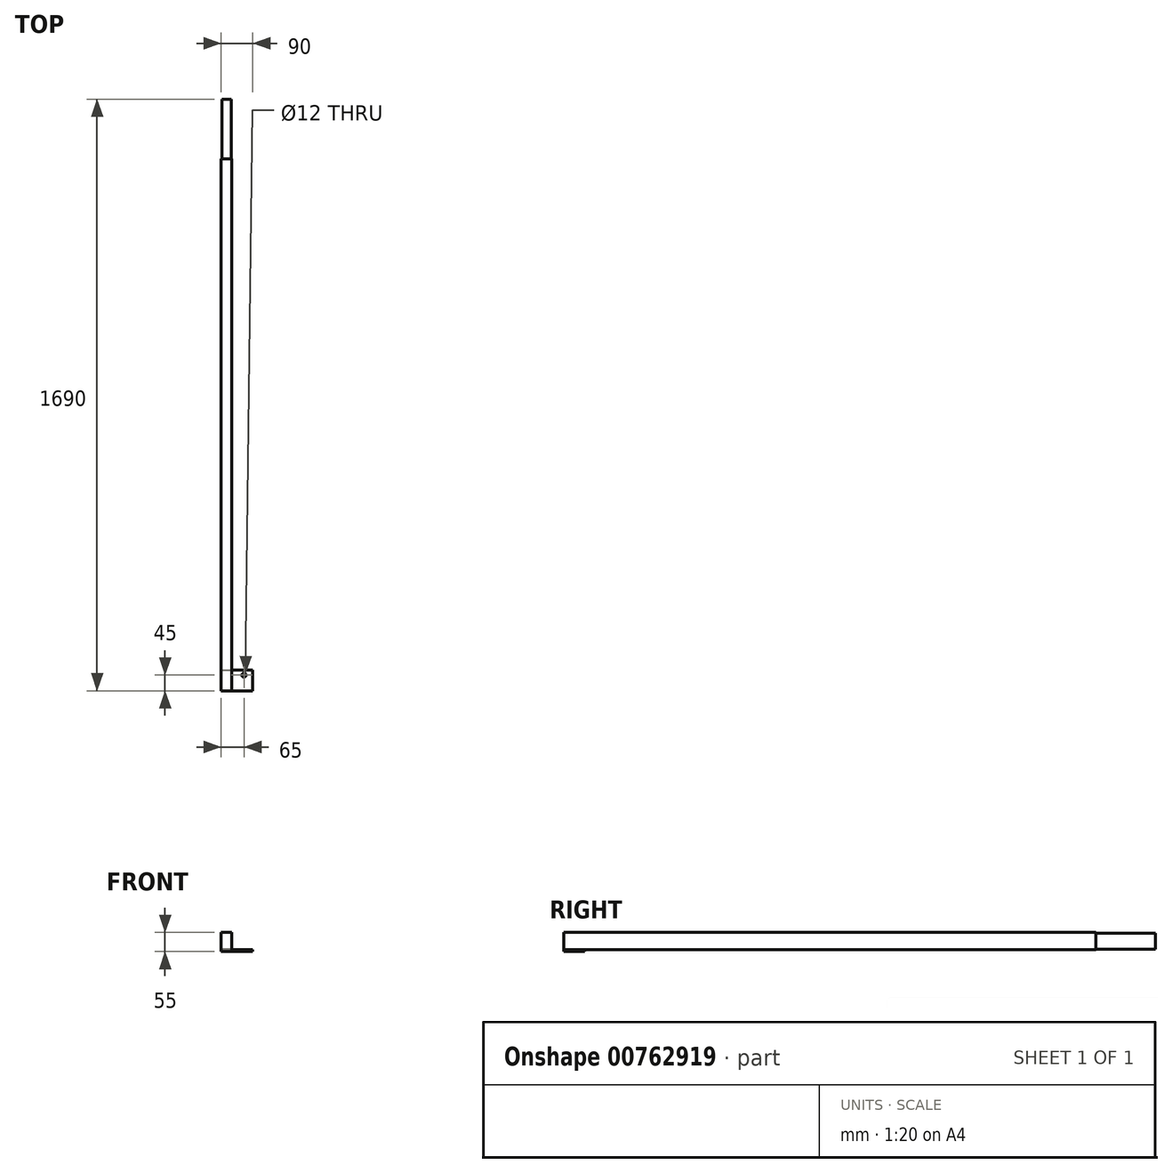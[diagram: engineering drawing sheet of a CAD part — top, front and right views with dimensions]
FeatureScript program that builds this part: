
annotation { "Feature Type Name" : "Feature", "Feature Type Description" : "" }
export const myFeature = defineFeature(function(context is Context, id is Id, definition is map)
    precondition{}
    {
        {
            var Q0;
            Q0=qCreatedBy(makeId("Front.planeOp"),FACE);
            var sketch = newSketch(context, id + "F0", { "sketchPlane" : qUnion([Q0])});
            skLineSegment(sketch, "E0.bottom", {"start": v(13, -23) * mm, "end": v(-13, -23) * mm});
            skLineSegment(sketch, "E0.top", {"start": v(13, 23) * mm, "end": v(-13, 23) * mm});
            skLineSegment(sketch, "E0.left", {"start": v(13, -23) * mm, "end": v(13, 23) * mm});
            skLineSegment(sketch, "E0.right", {"start": v(-13, -23) * mm, "end": v(-13, 23) * mm});
            skPoint(sketch, "E0.middle", {"position": v(0, 0) * mm});
            skSolve(sketch);
        }
        {
            var Q0;
            Q0 = qSketchRegion(id + "F0", true);
            extrude(context, id + "F1", {"entities" : qUnion([Q0]), "depth" : 170 * mm, "offsetDistance" : 25 * mm});
        }
        {
            var Q0;
            Q0=makeQuery(id+"F1.opExtrude","CAP_FACE",FACE,{"disambiguationData":[OSD([sQuery(id+"F0.wireOp",EDGE,"E0.bottom"),sQuery(id+"F0.wireOp",EDGE,"E0.top"),sQuery(id+"F0.wireOp",EDGE,"E0.left"),sQuery(id+"F0.wireOp",EDGE,"E0.right")])],"isStart":false});
            var sketch = newSketch(context, id + "F2", { "sketchPlane" : qUnion([Q0])});
            skLineSegment(sketch, "E1.bottom", {"start": v(15, -25) * mm, "end": v(-15, -25) * mm});
            skLineSegment(sketch, "E1.top", {"start": v(15, 25) * mm, "end": v(-15, 25) * mm});
            skLineSegment(sketch, "E1.left", {"start": v(15, -25) * mm, "end": v(15, 25) * mm});
            skLineSegment(sketch, "E1.right", {"start": v(-15, -25) * mm, "end": v(-15, 25) * mm});
            skPoint(sketch, "E1.middle", {"position": v(0, 0) * mm});
            skSolve(sketch);
        }
        {
            var Q0;
            Q0 = qSketchRegion(id + "F2", true);
            extrude(context, id + "F3", {"entities" : qUnion([Q0]), "operationType" : NewBodyOperationType.ADD, "depth" : 1520 * mm, "offsetDistance" : 25 * mm});
        }
        {
            var Q0;
            Q0=makeQuery(id+"F3.opExtrude","SWEPT_FACE",FACE,{"disambiguationData":[OSD([sQuery(id+"F2.wireOp",EDGE,"E1.bottom")])]});
            var sketch = newSketch(context, id + "F4", { "sketchPlane" : qUnion([Q0])});
            skLineSegment(sketch, "E2.bottom", {"start": v(-15, 1690) * mm, "end": v(15, 1690) * mm});
            skLineSegment(sketch, "E2.top", {"start": v(-15, 1630) * mm, "end": v(15, 1630) * mm});
            skLineSegment(sketch, "E2.left", {"start": v(-15, 1690) * mm, "end": v(-15, 1630) * mm});
            skLineSegment(sketch, "E2.right", {"start": v(15, 1690) * mm, "end": v(15, 1630) * mm});
            skLineSegment(sketch, "E3.bottom", {"start": v(15, 1690) * mm, "end": v(75, 1690) * mm});
            skLineSegment(sketch, "E3.top", {"start": v(15, 1630) * mm, "end": v(75, 1630) * mm});
            skLineSegment(sketch, "E3.right", {"start": v(75, 1690) * mm, "end": v(75, 1630) * mm});
            skLineSegment(sketch, "E4", {"start": v(15, 1645) * mm, "end": v(50, 1645) * mm});
            skCircle(sketch, "E5", {"center": v(50, 1645) * mm, "radius": 6 * mm});
            skSolve(sketch);
        }
        {
            var Q0;
            Q0 = qSketchRegion(id + "F4", true);
            extrude(context, id + "F5", {"entities" : qUnion([Q0]), "operationType" : NewBodyOperationType.ADD, "depth" : 5 * mm, "offsetDistance" : 25 * mm});
        }
    });
